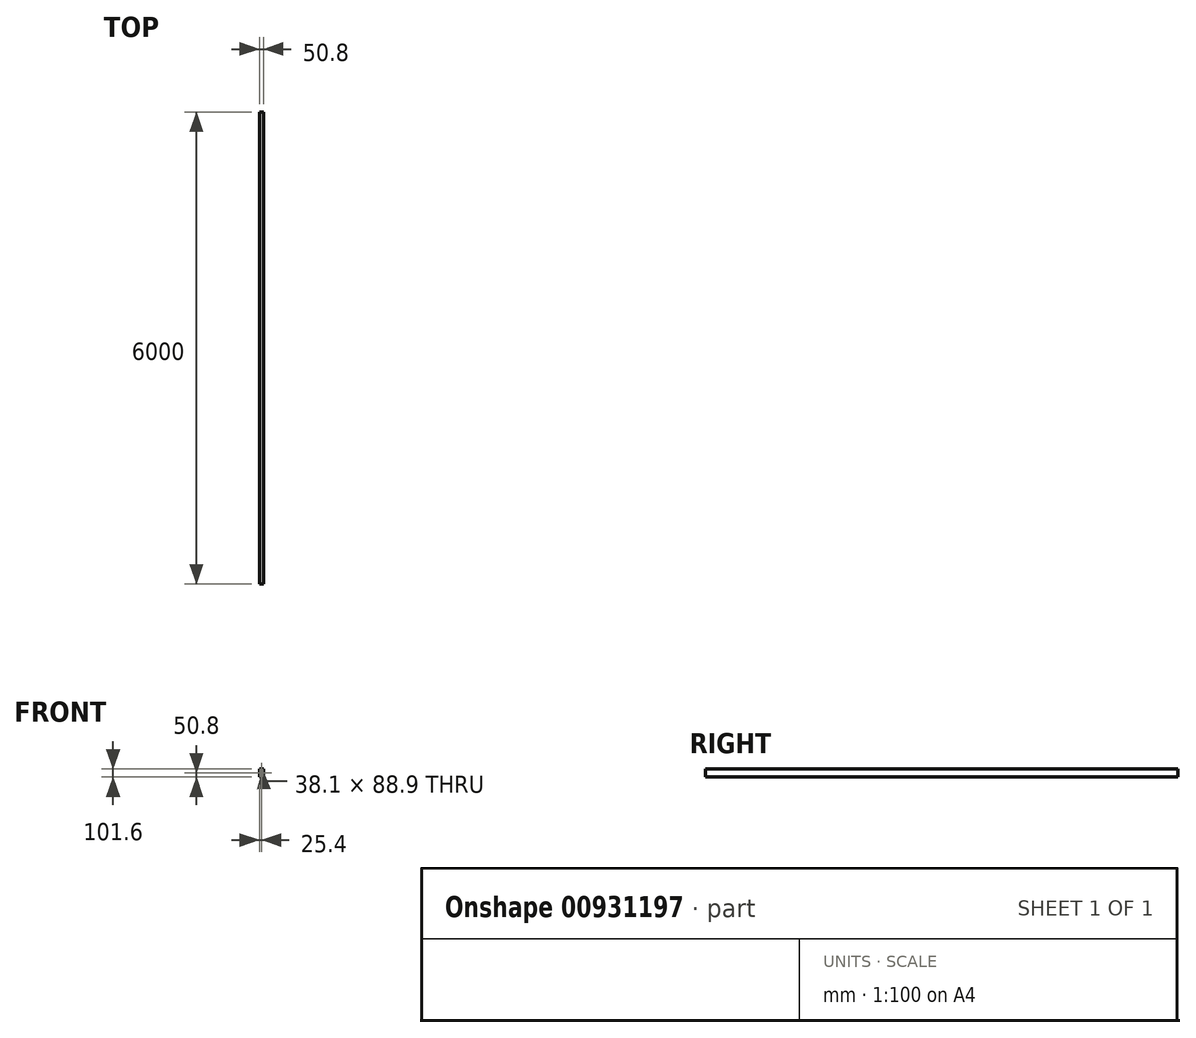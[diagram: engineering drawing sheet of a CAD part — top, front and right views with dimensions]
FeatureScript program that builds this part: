
annotation { "Feature Type Name" : "Feature", "Feature Type Description" : "" }
export const myFeature = defineFeature(function(context is Context, id is Id, definition is map)
    precondition{}
    {
        {
            var Q0;
            Q0=qCreatedBy(makeId("Front.planeOp"),FACE);
            var sketch = newSketch(context, id + "F0", { "sketchPlane" : qUnion([Q0])});
            skLineSegment(sketch, "E0.bottom", {"start": v(0, 0) * mm, "end": v(50.8, 0) * mm});
            skLineSegment(sketch, "E0.top", {"start": v(0, 101.6) * mm, "end": v(50.8, 101.6) * mm});
            skLineSegment(sketch, "E0.left", {"start": v(0, 0) * mm, "end": v(0, 101.6) * mm});
            skLineSegment(sketch, "E0.right", {"start": v(50.8, 0) * mm, "end": v(50.8, 101.6) * mm});
            skLineSegment(sketch, "E1.bottom", {"start": v(6.35, 95.25) * mm, "end": v(44.45, 95.25) * mm});
            skLineSegment(sketch, "E1.top", {"start": v(6.35, 6.35) * mm, "end": v(44.45, 6.35) * mm});
            skLineSegment(sketch, "E1.left", {"start": v(6.35, 95.25) * mm, "end": v(6.35, 6.35) * mm});
            skLineSegment(sketch, "E1.right", {"start": v(44.45, 95.25) * mm, "end": v(44.45, 6.35) * mm});
            skSolve(sketch);
        }
        {
            var Q0;
            Q0=makeQuery(id+"F0.imprint","IMPRINT",FACE,{"disambiguationData":[TD([[makeQuery(id+"F0.imprint","IMPRINT",EDGE,{"derivedFrom":sQuery(id+"F0.wireOp",EDGE,"E0.bottom")}),1.0]])]});
            extrude(context, id + "F1", {"entities" : qUnion([Q0]), "oppositeDirection" : true, "depth" : 6000 * mm, "offsetDistance" : 25.4 * mm});
        }
    });
